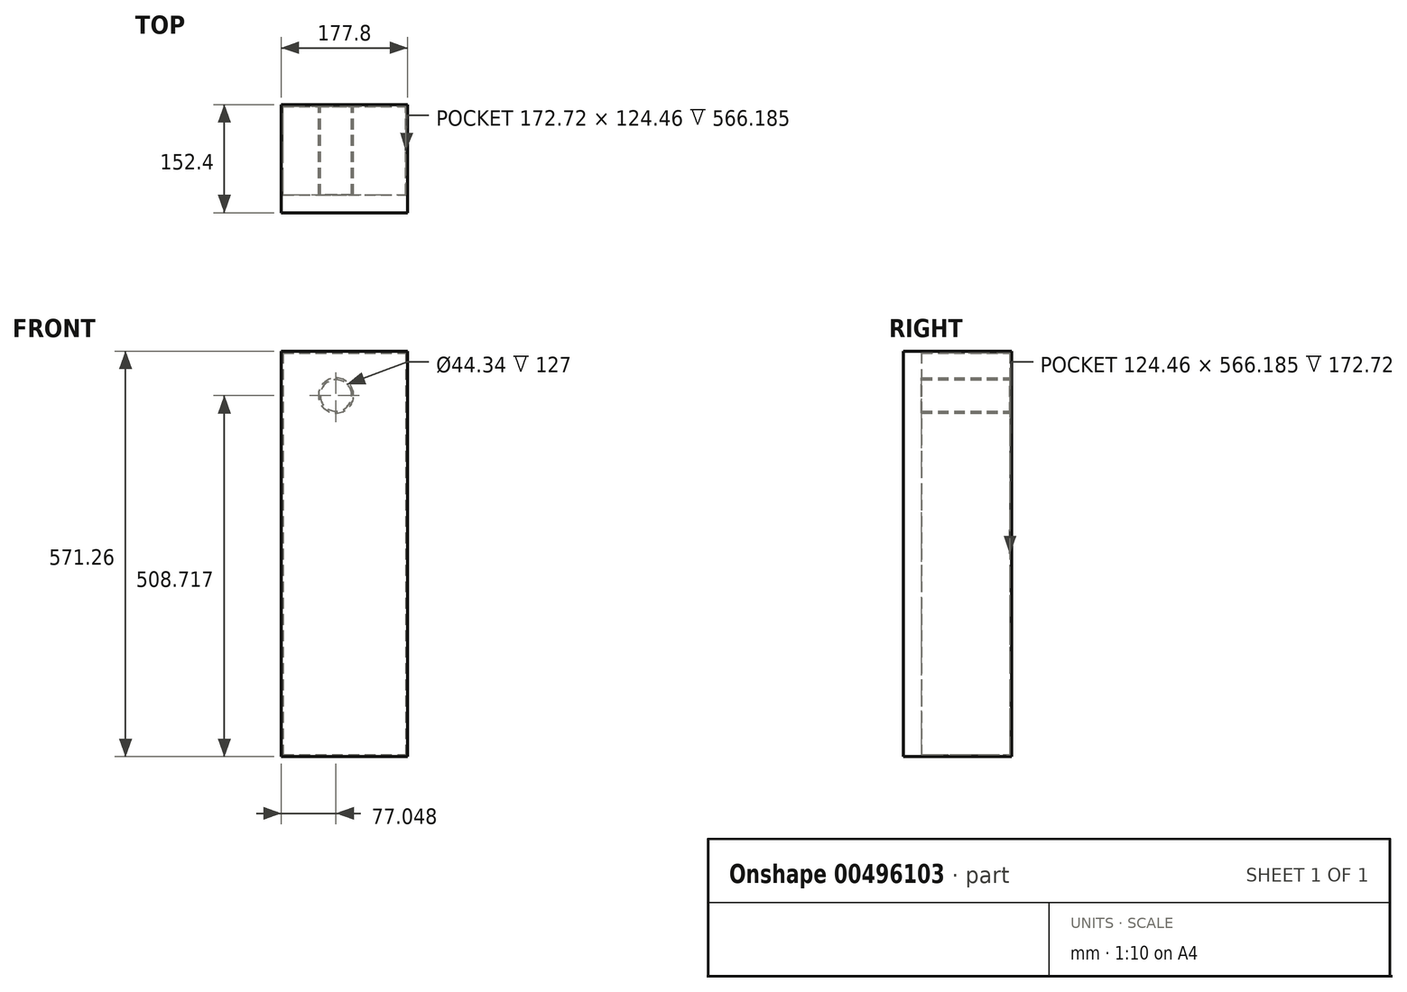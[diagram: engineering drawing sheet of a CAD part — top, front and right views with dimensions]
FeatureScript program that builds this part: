
annotation { "Feature Type Name" : "Feature", "Feature Type Description" : "" }
export const myFeature = defineFeature(function(context is Context, id is Id, definition is map)
    precondition{}
    {
        {
            var Q0;
            Q0=qCreatedBy(makeId("Front.planeOp"),FACE);
            var sketch = newSketch(context, id + "F0", { "sketchPlane" : qUnion([Q0])});
            skLineSegment(sketch, "E0.bottom", {"start": v(-88.9, 285.63) * mm, "end": v(88.9, 285.63) * mm});
            skLineSegment(sketch, "E0.top", {"start": v(-88.9, -285.63) * mm, "end": v(88.9, -285.63) * mm});
            skLineSegment(sketch, "E0.left", {"start": v(-88.9, 285.63) * mm, "end": v(-88.9, -285.63) * mm});
            skLineSegment(sketch, "E0.right", {"start": v(88.9, 285.63) * mm, "end": v(88.9, -285.63) * mm});
            skPoint(sketch, "E0.middle", {"position": v(0, 0) * mm});
            skLineSegment(sketch, "E1.top", {"start": v(-88.9, 145.57) * mm, "end": v(88.9, 145.57) * mm});
            skLineSegment(sketch, "E1.left", {"start": v(-88.9, 285.63) * mm, "end": v(-88.9, 145.57) * mm});
            skLineSegment(sketch, "E1.right", {"start": v(88.9, 285.63) * mm, "end": v(88.9, 145.57) * mm});
            skCircle(sketch, "E2", {"center": v(-11.85, 223.09) * mm, "radius": 22.17 * mm});
            skSolve(sketch);
        }
        {
            var Q0;
            Q0 = qSketchRegion(id + "F0", true);
            extrude(context, id + "F1", {"entities" : qUnion([Q0]), "depth" : 127 * mm});
        }
        {
            var Q0;
            Q0=makeQuery(id+"F1.opExtrude","CAP_FACE",FACE,{"disambiguationData":[OSD([sQuery(id+"F0.wireOp",EDGE,"E0.top"),sQuery(id+"F0.wireOp",EDGE,"E0.left"),sQuery(id+"F0.wireOp",EDGE,"E0.right"),sQuery(id+"F0.wireOp",EDGE,"E0.bottom"),sQuery(id+"F0.wireOp",EDGE,"E1.left"),sQuery(id+"F0.wireOp",EDGE,"E1.right"),sQuery(id+"F0.wireOp",EDGE,"E2")])],"isStart":false});
            shell(context, id + "F2", {"entities" : qUnion([Q0]), "thickness" : 2.54 * mm});
        }
        {
            var Q0;
            {var subQ0=sQuery(id+"F0.wireOp",EDGE,"E2");var subQ1=sQuery(id+"F0.wireOp",EDGE,"E1.right");var subQ2=sQuery(id+"F0.wireOp",EDGE,"E1.left");var subQ3=sQuery(id+"F0.wireOp",EDGE,"E0.bottom");var subQ4=sQuery(id+"F0.wireOp",EDGE,"E0.right");var subQ5=sQuery(id+"F0.wireOp",EDGE,"E0.left");var subQ6=sQuery(id+"F0.wireOp",EDGE,"E0.top");Q0=makeQuery(id+"F2.opShell","OFFSET_FACE",FACE,{"disambiguationData":[OSD([subQ6,subQ5,subQ4,subQ3,subQ2,subQ1,subQ0]),TDD([makeQuery(id+"F1.opExtrude","CAP_FACE",FACE,{"disambiguationData":[OSD([subQ6,subQ5,subQ4,subQ3,subQ2,subQ1,subQ0])],"isStart":false})])]});}
            var sketch = newSketch(context, id + "F3", { "sketchPlane" : qUnion([Q0])});
            skLineSegment(sketch, "E3.bottom", {"start": v(-88.9, 285.63) * mm, "end": v(88.9, 285.63) * mm});
            skLineSegment(sketch, "E3.top", {"start": v(-88.9, -285.63) * mm, "end": v(88.9, -285.63) * mm});
            skLineSegment(sketch, "E3.left", {"start": v(-88.9, 285.63) * mm, "end": v(-88.9, -285.63) * mm});
            skLineSegment(sketch, "E3.right", {"start": v(88.9, 285.63) * mm, "end": v(88.9, -285.63) * mm});
            skSolve(sketch);
        }
        {
            var Q0;
            Q0 = qSketchRegion(id + "F3", true);
            extrude(context, id + "F4", {"entities" : qUnion([Q0]), "operationType" : NewBodyOperationType.ADD, "depth" : 25.4 * mm});
        }
    });
